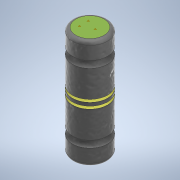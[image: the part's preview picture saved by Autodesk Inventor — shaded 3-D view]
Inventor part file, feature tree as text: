
AUTODESK INVENTOR PART (.ipt)
format: ipt  version: 2020 (Build 240168000, 168)  size: 207,872 bytes
history: native  units: mm
features: other x9, sketch x4, plane x3, revolve x2, extrude x1, fillet x1, projected_geometry x1
ambient origin geometry x8: Origin, YZ Plane, XZ Plane, XY Plane, X Axis, Y Axis, Z Axis, Center Point
bodies: Body1 (feature_tree)
feature tree (21):
  other  "Sólido1"
  extrude  "Extrusión1"  Depth=63.1mm TaperAngle=0.0deg
  plane  "Plano de trabajo1"
  plane  "Plano de trabajo2"
  sketch  "Boceto2"  dims[d3=0.0mm d4=1.5mm]
  other  "Eje de trabajo1"
  revolve  "Revolución1"  [1 undecoded]
  revolve  "Revolución2"  [1 undecoded]
  fillet  "Empalme1"  Radius=1.7mm
  sketch  "Boceto4"  dims[d8=0.0mm d9=90.0deg d10=4.0mm d11=20.0mm d12=4.0mm d13=20.0mm d14=90.0deg d15=2.0mm]
  other  "Eje de trabajo2"
  other  "+ext"
  other  "-ext"
  other  "Neutroext"
  other  "+int"
  other  "-int"
  other  "Neutroint"
  sketch  "Boceto1"  dims[d0=20.3mm d1=63.1mm d2=0.0mm]
  projected_geometry  "Contorno proyectado1"
  plane  "Plano de trabajo3"
  sketch  "Boceto3"  dims[d5=1.7mm d6=1.5mm d7=1.7mm]
note: 2 required parameter values undecoded (feature->parameter linkage not recoverable at this tier; creation-order binding heuristic only, values carry confidence <= 0.55)
